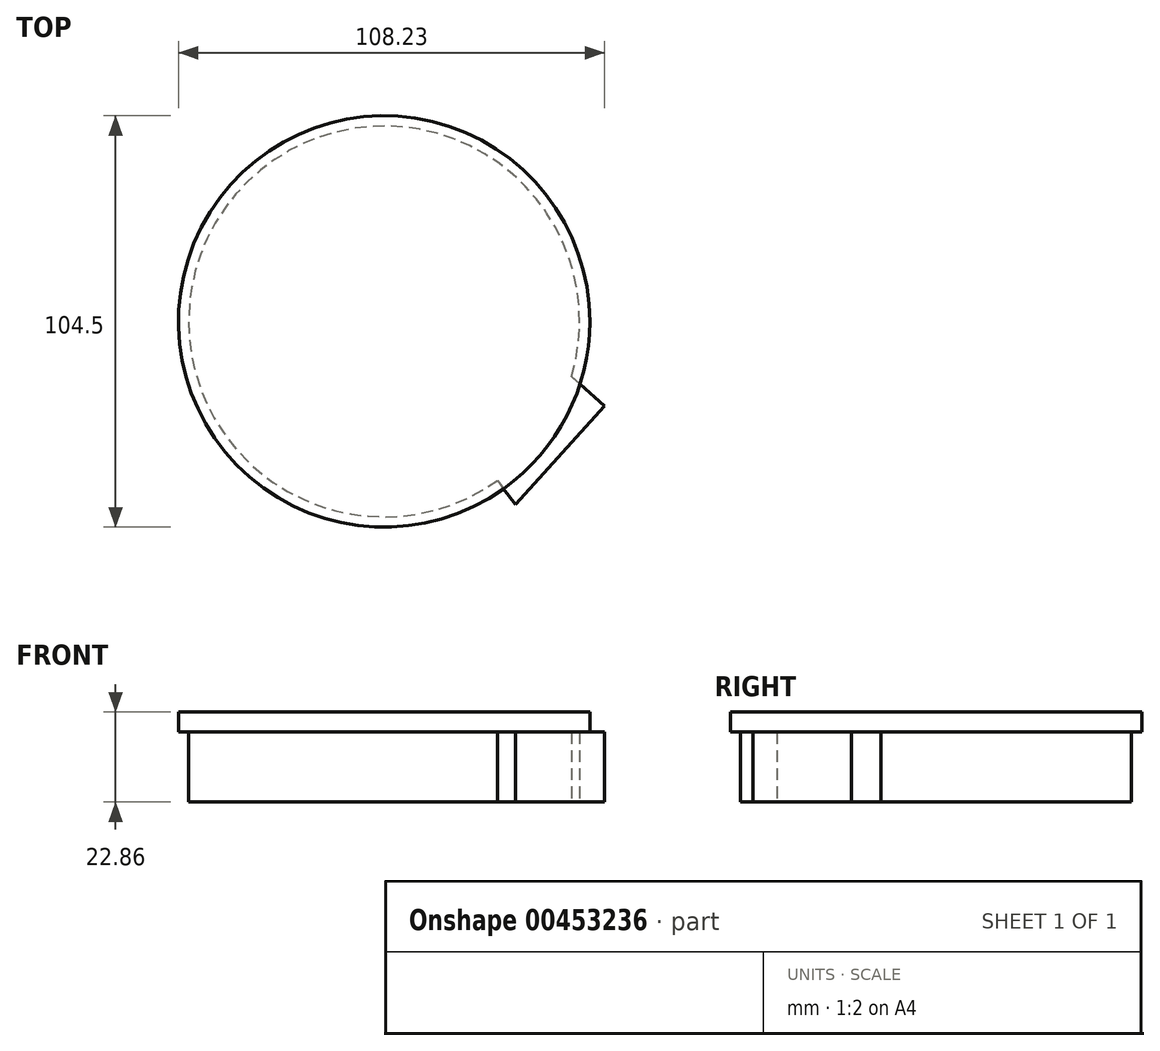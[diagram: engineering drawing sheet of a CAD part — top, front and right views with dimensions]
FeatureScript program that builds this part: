
annotation { "Feature Type Name" : "Feature", "Feature Type Description" : "" }
export const myFeature = defineFeature(function(context is Context, id is Id, definition is map)
    precondition{}
    {
        {
            var Q0;
            Q0=qCreatedBy(makeId("Top.planeOp"),FACE);
            var sketch = newSketch(context, id + "F0", { "sketchPlane" : qUnion([Q0])});
            skCircle(sketch, "E0", {"center": v(0, 0) * mm, "radius": 49.65 * mm});
            skSolve(sketch);
        }
        {
            var Q0;
            Q0=makeQuery(id+"F0.imprint","IMPRINT",FACE,{"disambiguationData":[TD([[makeQuery(id+"F0.imprint","IMPRINT",EDGE,{"derivedFrom":sQuery(id+"F0.wireOp",EDGE,"E0")}),1.0]])]});
            extrude(context, id + "F1", {"entities" : qUnion([Q0]), "depth" : 17.78 * mm});
        }
        {
            var Q0;
            Q0=makeQuery(id+"F1.opExtrude","CAP_FACE",FACE,{"disambiguationData":[OSD([sQuery(id+"F0.wireOp",EDGE,"E0")])],"isStart":false});
            var sketch = newSketch(context, id + "F2", { "sketchPlane" : qUnion([Q0])});
            skCircle(sketch, "E1", {"center": v(0, 0) * mm, "radius": 52.25 * mm});
            skSolve(sketch);
        }
        {
            var Q0;
            Q0 = qSketchRegion(id + "F2", true);
            extrude(context, id + "F3", {"entities" : qUnion([Q0]), "operationType" : NewBodyOperationType.ADD, "depth" : 5.08 * mm});
        }
        {
            var Q0;
            Q0=qCreatedBy(makeId("Top.planeOp"),FACE);
            var sketch = newSketch(context, id + "F4", { "sketchPlane" : qUnion([Q0])});
            skLineSegment(sketch, "E2", {"start": v(24.62, -34.78) * mm, "end": v(33.42, -46.56) * mm});
            skLineSegment(sketch, "E3", {"start": v(33.42, -46.56) * mm, "end": v(55.98, -21.48) * mm});
            skLineSegment(sketch, "E4", {"start": v(55.98, -21.48) * mm, "end": v(46.19, -12.67) * mm});
            skLineSegment(sketch, "E5", {"start": v(46.19, -12.67) * mm, "end": v(24.62, -34.78) * mm});
            skSolve(sketch);
        }
        {
            var Q0;
            Q0=makeQuery(id+"F4.imprint","IMPRINT",FACE,{"disambiguationData":[TD([[makeQuery(id+"F4.imprint","IMPRINT",EDGE,{"derivedFrom":sQuery(id+"F4.wireOp",EDGE,"E2")}),1.0]])]});
            extrude(context, id + "F5", {"entities" : qUnion([Q0]), "operationType" : NewBodyOperationType.ADD, "depth" : 17.78 * mm});
        }
    });
